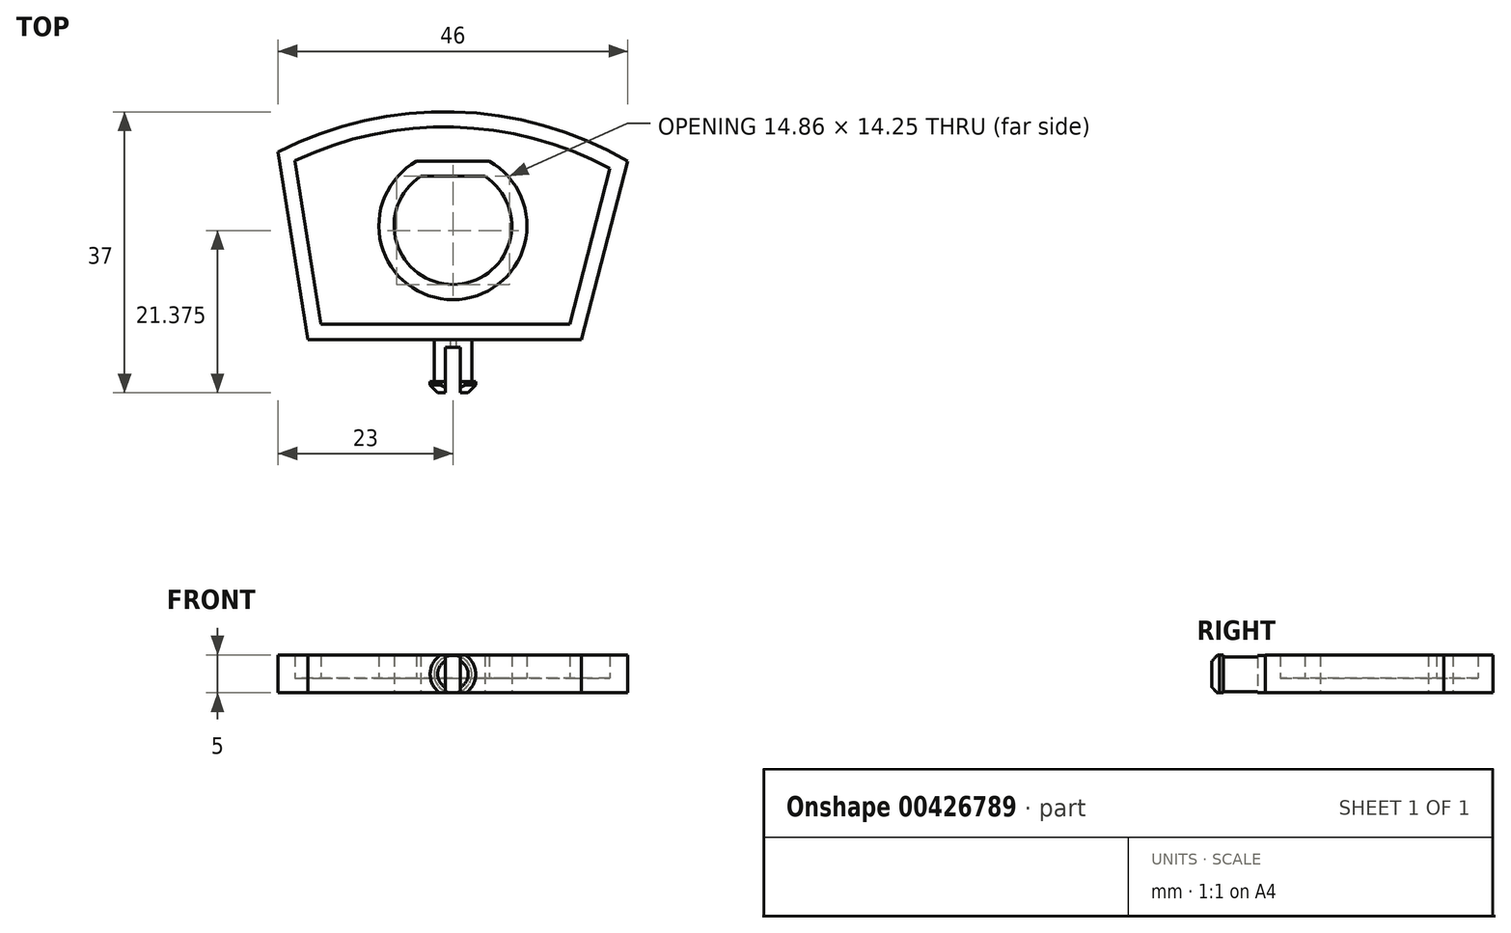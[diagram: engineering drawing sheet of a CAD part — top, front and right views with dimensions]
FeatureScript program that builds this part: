
annotation { "Feature Type Name" : "Feature", "Feature Type Description" : "" }
export const myFeature = defineFeature(function(context is Context, id is Id, definition is map)
    precondition{}
    {
        {
            var Q0;
            Q0=qCreatedBy(makeId("Top.planeOp"),FACE);
            var sketch = newSketch(context, id + "F0", { "sketchPlane" : qUnion([Q0])});
            skLineSegment(sketch, "E0", {"start": v(-23, 24.7) * mm, "end": v(-19.08, 0) * mm});
            skLineSegment(sketch, "E1", {"start": v(16.92, 0) * mm, "end": v(23, 23.53) * mm});
            skArc(sketch, "E2", {"start": v(23, 23.53) * mm, "mid": v(0.15, 29.98) * mm, "end": v(-23, 24.7) * mm});
            skLineSegment(sketch, "E3", {"start": v(-19.08, 0) * mm, "end": v(16.92, 0) * mm});
            skSolve(sketch);
        }
        {
            var Q0;
            Q0 = qSketchRegion(id + "F0", true);
            extrude(context, id + "F1", {"entities" : qUnion([Q0]), "depth" : 5 * mm});
        }
        {
            var Q0;
            Q0=qCreatedBy(makeId("Top.planeOp"),FACE);
            var sketch = newSketch(context, id + "F2", { "sketchPlane" : qUnion([Q0])});
            skLineSegment(sketch, "E4", {"start": v(-4.22, 21.5) * mm, "end": v(4.22, 21.5) * mm});
            skArc(sketch, "E5", {"start": v(-4.22, 21.5) * mm, "mid": v(0, 7.25) * mm, "end": v(4.22, 21.5) * mm});
            skSolve(sketch);
        }
        {
            var Q0;
            Q0 = qSketchRegion(id + "F2", true);
            var Q1;
            Q1=sQuery(id+"F2.wireOp",EDGE,"E4");
            var Q2;
            Q2=sQuery(id+"F2.wireOp",EDGE,"E5");
            extrude(context, id + "F3", {"entities" : qUnion([Q0]), "operationType" : NewBodyOperationType.REMOVE, "surfaceEntities" : qUnion([Q1, Q2]), "endBound" : BoundingType.UP_TO_NEXT, "depth" : 25 * mm});
        }
        {
            var Q0;
            Q0=makeQuery(id+"F1.opExtrude","CAP_FACE",FACE,{"disambiguationData":[OSD([sQuery(id+"F0.wireOp",EDGE,"E0"),sQuery(id+"F0.wireOp",EDGE,"E1"),sQuery(id+"F0.wireOp",EDGE,"E2"),sQuery(id+"F0.wireOp",EDGE,"E3")])],"isStart":false});
            shell(context, id + "F4", {"entities" : qUnion([Q0]), "thickness" : 2 * mm});
        }
        {
            var Q0;
            Q0=qCreatedBy(makeId("Right.planeOp"),FACE);
            var sketch = newSketch(context, id + "F5", { "sketchPlane" : qUnion([Q0])});
            skLineSegment(sketch, "E6", {"start": v(0, 4.98) * mm, "end": v(-5.5, 4.98) * mm});
            skLineSegment(sketch, "E7", {"start": v(-5.5, 4.98) * mm, "end": v(-5.5, 5.5) * mm});
            skLineSegment(sketch, "E8", {"start": v(-5.5, 5.5) * mm, "end": v(-7, 5.5) * mm});
            skLineSegment(sketch, "E9", {"start": v(-7, 5.5) * mm, "end": v(-7, 2.5) * mm});
            skLineSegment(sketch, "E10", {"start": v(-7, 2.5) * mm, "end": v(0, 2.5) * mm});
            skLineSegment(sketch, "E11", {"start": v(0, 2.5) * mm, "end": v(0, 4.98) * mm});
            skSolve(sketch);
        }
        {
            var Q0;
            Q0=makeQuery(id+"F5.imprint","IMPRINT",FACE,{"disambiguationData":[TD([[makeQuery(id+"F5.imprint","IMPRINT",EDGE,{"derivedFrom":sQuery(id+"F5.wireOp",EDGE,"E6")}),1.0]])]});
            var Q1;
            Q1=sQuery(id+"F5.wireOp",EDGE,"E10");
            revolve(context, id + "F6", {"operationType" : NewBodyOperationType.ADD, "entities" : qUnion([Q0]), "axis" : qUnion([Q1]), "revolveType" : RevolveType.FULL});
        }
        {
            var Q0;
            Q0=makeQuery(id+"F6.opRevolve","SWEPT_FACE",FACE,{"disambiguationData":[OSD([sQuery(id+"F5.wireOp",EDGE,"E9")])]});
            chamfer(context, id + "F7", {"entities" : qUnion([Q0]), "width" : 1 * mm, "tangentPropagation" : true});
        }
        {
            var Q0;
            Q0=makeQuery(id+"F6.opRevolve","SWEPT_FACE",FACE,{"disambiguationData":[OSD([sQuery(id+"F5.wireOp",EDGE,"E9")])]});
            var sketch = newSketch(context, id + "F8", { "sketchPlane" : qUnion([Q0])});
            skLineSegment(sketch, "E12.bottom", {"start": v(-24.9, 0.05) * mm, "end": v(26.3, 0.05) * mm});
            skLineSegment(sketch, "E12.top", {"start": v(-24.9, 5.05) * mm, "end": v(26.3, 5.05) * mm});
            skLineSegment(sketch, "E12.left", {"start": v(-24.9, 0.05) * mm, "end": v(-24.9, 5.05) * mm});
            skLineSegment(sketch, "E12.right", {"start": v(26.3, 0.05) * mm, "end": v(26.3, 5.05) * mm});
            skSolve(sketch);
        }
        {
            var Q0;
            Q0 = qSketchRegion(id + "F8", true);
            extrude(context, id + "F9", {"entities" : qUnion([Q0]), "operationType" : NewBodyOperationType.INTERSECT, "endBound" : BoundingType.THROUGH_ALL, "oppositeDirection" : true, "depth" : 25 * mm});
        }
        {
            var Q0;
            Q0=makeQuery(id+"F6.opRevolve","SWEPT_FACE",FACE,{"disambiguationData":[OSD([sQuery(id+"F5.wireOp",EDGE,"E9")])]});
            var sketch = newSketch(context, id + "F10", { "sketchPlane" : qUnion([Q0])});
            skLineSegment(sketch, "E13.bottom", {"start": v(-1, 6.1) * mm, "end": v(1, 6.1) * mm});
            skLineSegment(sketch, "E13.top", {"start": v(-1, -0.75) * mm, "end": v(1, -0.75) * mm});
            skLineSegment(sketch, "E13.left", {"start": v(-1, 6.1) * mm, "end": v(-1, -0.75) * mm});
            skLineSegment(sketch, "E13.right", {"start": v(1, 6.1) * mm, "end": v(1, -0.75) * mm});
            skSolve(sketch);
        }
        {
            var Q0;
            Q0 = qSketchRegion(id + "F10", true);
            extrude(context, id + "F11", {"entities" : qUnion([Q0]), "operationType" : NewBodyOperationType.REMOVE, "oppositeDirection" : true, "depth" : 6 * mm});
        }
    });
